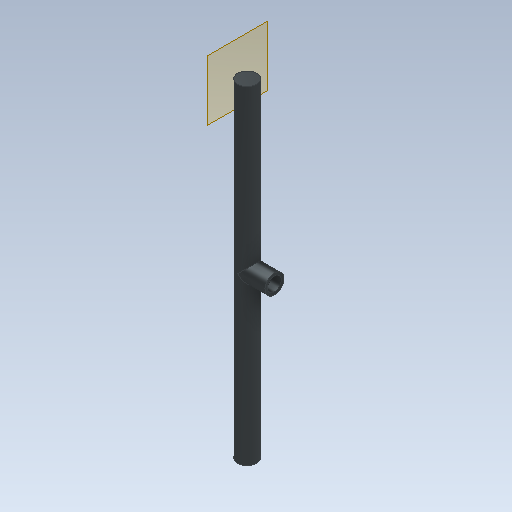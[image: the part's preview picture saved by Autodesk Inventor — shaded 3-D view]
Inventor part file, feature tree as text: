
AUTODESK INVENTOR PART (.ipt)
format: ipt  version: 2020.2 (Build 242310000, 310)  size: 181,248 bytes
history: native  units: in
note: dims shown in document units (in); Inventor stores cm internally (conversion verified against a paired STEP export)
features: sketch x9, extrude x6, plane x2
ambient origin geometry x8: Origin, YZ Plane, XZ Plane, XY Plane, X Axis, Y Axis, Z Axis, Center Point
bodies: Solid1 (feature_tree)
feature tree (17):
  sketch  "Sketch1"  dims[d0=0.1969in d1=0.2756in]
  extrude  "Extrusion1"  Depth=0.2756in
  extrude  "Extrusion2"  Depth=0.1969in TaperAngle=0.0deg
  extrude  "Extrusion3"  Depth=0.1969in
  sketch  "Sketch5"  dims[d12=0.0394in d13=0.0394in]
  extrude  "Extrusion4"  Depth=0.3937in TaperAngle=0.0deg
  sketch  "Sketch7"  dims[d16=0.0394in]
  plane  "Work Plane5"
  extrude  "Extrusion5"  Depth=0.0394in
  plane  "Work Plane7"
  extrude  "Extrusion6"  Depth=0.0394in
  sketch  "Sketch2"  dims[d2=4.3307in d3=0.0in d4=0.1969in d5=0.0in]
  sketch  "Sketch3"  dims[d6=0.1969in d7=0.0in d8=0.1969in]
  sketch  "Sketch4"  dims[d9=0.2756in d10=0.3937in d11=0.0in]
  sketch  "Sketch6"  dims[d14=0.0394in d15=0.0394in]
  sketch  "Sketch8"  dims[d17=0.1181in d18=0.0in]
  sketch  "Sketch9"  dims[d19=0.0394in d20=0.0394in d21=0.0394in d22=0.0394in d23=0.0394in d24=0.0394in d25=0.1181in d26=0.0in]
